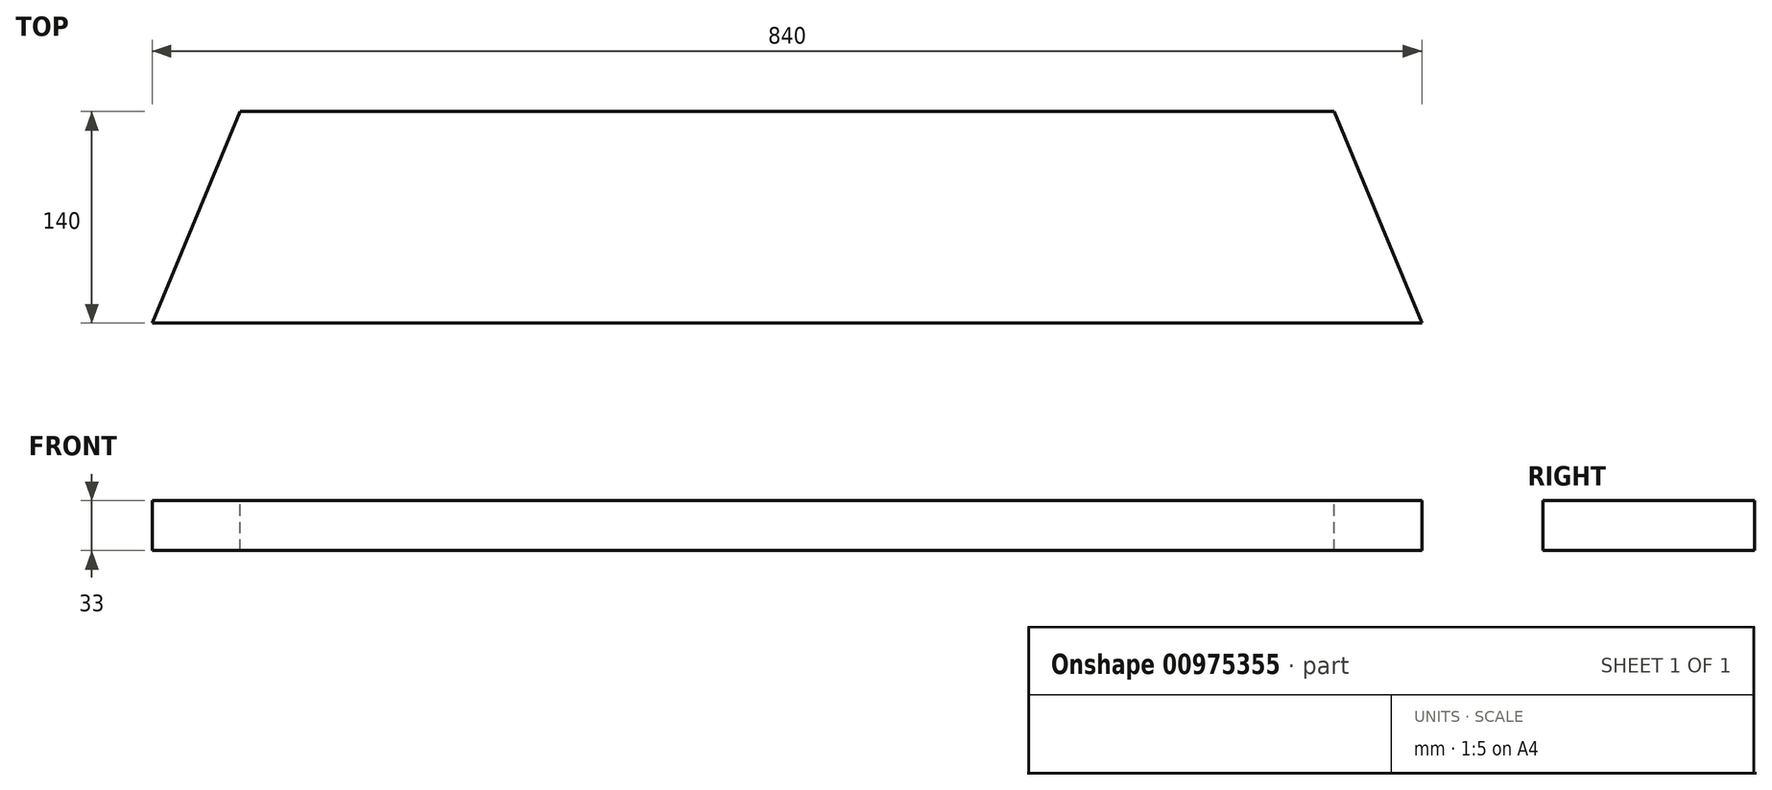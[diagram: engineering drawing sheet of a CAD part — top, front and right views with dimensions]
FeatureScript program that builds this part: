
annotation { "Feature Type Name" : "Feature", "Feature Type Description" : "" }
export const myFeature = defineFeature(function(context is Context, id is Id, definition is map)
    precondition{}
    {
        {
            var Q0;
            Q0=qCreatedBy(makeId("Top.planeOp"),FACE);
            var sketch = newSketch(context, id + "F0", { "sketchPlane" : qUnion([Q0])});
            skLineSegment(sketch, "E0.bottom", {"start": v(420, 70) * mm, "end": v(-420, 70) * mm});
            skLineSegment(sketch, "E0.top", {"start": v(420, -70) * mm, "end": v(-420, -70) * mm});
            skLineSegment(sketch, "E0.left", {"start": v(420, 70) * mm, "end": v(420, -70) * mm});
            skLineSegment(sketch, "E0.right", {"start": v(-420, 70) * mm, "end": v(-420, -70) * mm});
            skPoint(sketch, "E0.middle", {"position": v(0, 0) * mm});
            skSolve(sketch);
        }
        {
            var Q0;
            Q0=makeQuery(id+"F0.imprint","IMPRINT",FACE,{"disambiguationData":[TD([[makeQuery(id+"F0.imprint","IMPRINT",EDGE,{"derivedFrom":sQuery(id+"F0.wireOp",EDGE,"E0.bottom")}),1.0]])]});
            extrude(context, id + "F1", {"entities" : qUnion([Q0]), "endBound" : BoundingType.SYMMETRIC, "depth" : 33 * mm, "offsetDistance" : 25 * mm});
        }
        {
            var Q0;
            Q0=makeQuery(id+"F1.opExtrude","CAP_FACE",FACE,{"disambiguationData":[OSD([sQuery(id+"F0.wireOp",EDGE,"E0.bottom"),sQuery(id+"F0.wireOp",EDGE,"E0.top"),sQuery(id+"F0.wireOp",EDGE,"E0.left"),sQuery(id+"F0.wireOp",EDGE,"E0.right")])],"isStart":false});
            var sketch = newSketch(context, id + "F2", { "sketchPlane" : qUnion([Q0])});
            skLineSegment(sketch, "E1", {"start": v(-420, -70) * mm, "end": v(-362.01, 70) * mm});
            skLineSegment(sketch, "E2", {"start": v(-362.01, 70) * mm, "end": v(-420, 70) * mm});
            skLineSegment(sketch, "E3", {"start": v(-420, 70) * mm, "end": v(-420, -70) * mm});
            skLineSegment(sketch, "E4", {"start": v(420, 70) * mm, "end": v(362.01, 70) * mm});
            skLineSegment(sketch, "E5", {"start": v(362.01, 70) * mm, "end": v(420, -70) * mm});
            skLineSegment(sketch, "E6", {"start": v(420, -70) * mm, "end": v(420, 70) * mm});
            skSolve(sketch);
        }
        {
            var Q0;
            Q0 = qSketchRegion(id + "F2", true);
            extrude(context, id + "F3", {"entities" : qUnion([Q0]), "operationType" : NewBodyOperationType.REMOVE, "endBound" : BoundingType.THROUGH_ALL, "oppositeDirection" : true, "depth" : 25 * mm, "offsetDistance" : 25 * mm});
        }
    });
